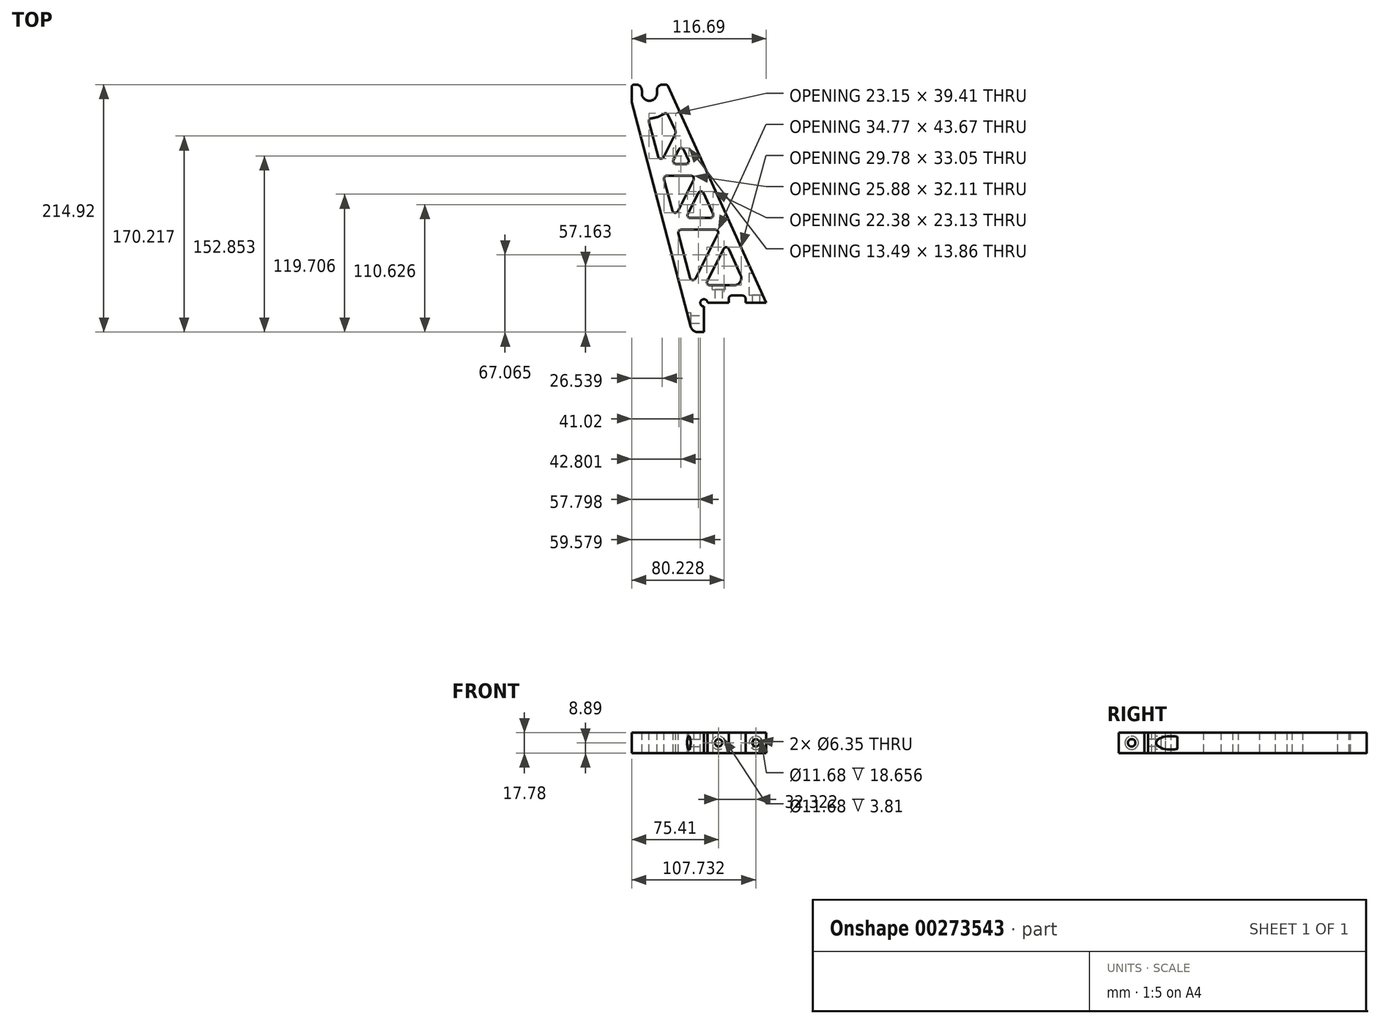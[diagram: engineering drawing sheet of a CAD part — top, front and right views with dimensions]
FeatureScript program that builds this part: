
annotation { "Feature Type Name" : "Feature", "Feature Type Description" : "" }
export const myFeature = defineFeature(function(context is Context, id is Id, definition is map)
    precondition{}
    {
        {
            var Q0;
            Q0=qCreatedBy(makeId("Top.planeOp"),FACE);
            var sketch = newSketch(context, id + "F0", { "sketchPlane" : qUnion([Q0])});
            skLineSegment(sketch, "E0", {"start": v(3.18, 0) * mm, "end": v(60.33, 0) * mm, "construction": true});
            skLineSegment(sketch, "E1", {"start": v(60.33, 0) * mm, "end": v(60.33, 190.5) * mm, "construction": true});
            skCircle(sketch, "E2", {"center": v(-47.28, 181.9) * mm, "radius": 101.6 * mm, "construction": true});
            skLineSegment(sketch, "E3.bottom", {"start": v(60.33, 0) * mm, "end": v(3.18, 0) * mm, "construction": true});
            skLineSegment(sketch, "E3.top", {"start": v(60.32, 220) * mm, "end": v(-79.68, 220) * mm, "construction": true});
            skLineSegment(sketch, "E3.left", {"start": v(60.33, 0) * mm, "end": v(60.33, 220) * mm, "construction": true});
            skLineSegment(sketch, "E3.right", {"start": v(-79.67, 0) * mm, "end": v(-79.68, 220) * mm, "construction": true});
            skArc(sketch, "E4", {"start": v(-53.82, 181.9) * mm, "mid": v(-47.28, 175.36) * mm, "end": v(-40.74, 181.9) * mm});
            skLineSegment(sketch, "E5", {"start": v(-53.82, 181.9) * mm, "end": v(-53.82, 184.44) * mm});
            skLineSegment(sketch, "E6", {"start": v(-40.74, 181.9) * mm, "end": v(-40.74, 184.44) * mm});
            skLineSegment(sketch, "E7", {"start": v(-35.66, 189.52) * mm, "end": v(-33.49, 189.52) * mm});
            skLineSegment(sketch, "E8", {"start": v(-31.18, 188.03) * mm, "end": v(53.98, 0) * mm});
            skLineSegment(sketch, "E9", {"start": v(53.98, 0) * mm, "end": v(36.07, 0) * mm});
            skLineSegment(sketch, "E10", {"start": v(36.07, 0) * mm, "end": v(36.07, 3.81) * mm});
            skLineSegment(sketch, "E11", {"start": v(33.53, 6.35) * mm, "end": v(24.13, 6.35) * mm});
            skLineSegment(sketch, "E12", {"start": v(21.59, 3.81) * mm, "end": v(21.59, 0) * mm});
            skLineSegment(sketch, "E13", {"start": v(21.59, 0) * mm, "end": v(3.18, 0) * mm});
            skLineSegment(sketch, "E14", {"start": v(0, -25.4) * mm, "end": v(-5.26, -25.4) * mm});
            skLineSegment(sketch, "E15", {"start": v(-11.4, -20.67) * mm, "end": v(-62.71, 174.28) * mm});
            skLineSegment(sketch, "E16", {"start": v(-62.71, 174.28) * mm, "end": v(-62.71, 186.98) * mm});
            skLineSegment(sketch, "E17", {"start": v(-60.17, 189.52) * mm, "end": v(-58.9, 189.52) * mm});
            skLineSegment(sketch, "E18", {"start": v(0, -3.18) * mm, "end": v(0, -25.4) * mm});
            skArc(sketch, "E19", {"start": v(3.18, 0) * mm, "mid": v(-2.25, 2.25) * mm, "end": v(0, -3.18) * mm});
            skLineSegment(sketch, "E20.trimOffspring", {"start": v(0, 0) * mm, "end": v(-79.67, 0) * mm, "construction": true});
            skPoint(sketch, "E21.visualSharp", {"position": v(-53.82, 189.52) * mm});
            skArc(sketch, "E21.filletArc", {"start": v(-53.82, 184.44) * mm, "mid": v(-55.31, 188.03) * mm, "end": v(-58.9, 189.52) * mm});
            skPoint(sketch, "E22.visualSharp", {"position": v(-40.74, 189.52) * mm});
            skArc(sketch, "E22.filletArc", {"start": v(-35.66, 189.52) * mm, "mid": v(-39.25, 188.03) * mm, "end": v(-40.74, 184.44) * mm});
            skPoint(sketch, "E23.visualSharp", {"position": v(-62.71, 189.52) * mm});
            skArc(sketch, "E23.filletArc", {"start": v(-60.17, 189.52) * mm, "mid": v(-61.97, 188.78) * mm, "end": v(-62.71, 186.98) * mm});
            skPoint(sketch, "E24.visualSharp", {"position": v(-31.85, 189.52) * mm});
            skArc(sketch, "E24.filletArc", {"start": v(-31.18, 188.03) * mm, "mid": v(-32.11, 189.11) * mm, "end": v(-33.49, 189.52) * mm});
            skPoint(sketch, "E25.visualSharp", {"position": v(-10.16, -25.4) * mm});
            skArc(sketch, "E25.filletArc", {"start": v(-11.4, -20.67) * mm, "mid": v(-9.14, -24.08) * mm, "end": v(-5.26, -25.4) * mm});
            skLineSegment(sketch, "E26", {"start": v(-47.66, 157.02) * mm, "end": v(-39.76, 127) * mm});
            skLineSegment(sketch, "E27", {"start": v(5.17, 15.24) * mm, "end": v(26.07, 15.24) * mm});
            skLineSegment(sketch, "E28", {"start": v(31.86, 24.2) * mm, "end": v(21.63, 46.8) * mm});
            skArc(sketch, "E29", {"start": v(-45.42, 160.2) * mm, "mid": v(-39.85, 161.43) * mm, "end": v(-34.78, 164.06) * mm});
            skLineSegment(sketch, "E30", {"start": v(-7.33, 21.2) * mm, "end": v(12.2, 59.81) * mm});
            skLineSegment(sketch, "E31", {"start": v(9.93, 63.5) * mm, "end": v(-19.76, 63.5) * mm});
            skLineSegment(sketch, "E32", {"start": v(17.05, 46.9) * mm, "end": v(2.9, 18.93) * mm});
            skLineSegment(sketch, "E33", {"start": v(-11.78, 73.66) * mm, "end": v(5.53, 73.66) * mm});
            skLineSegment(sketch, "E34", {"start": v(-22.7, 79.63) * mm, "end": v(-9.02, 106.68) * mm});
            skLineSegment(sketch, "E35", {"start": v(-14.05, 77.35) * mm, "end": v(-4.92, 95.4) * mm});
            skLineSegment(sketch, "E36", {"start": v(0, 13.2) * mm, "end": v(-31.6, 133.28) * mm, "construction": true});
            skLineSegment(sketch, "E37", {"start": v(-11.29, 110.36) * mm, "end": v(-32.09, 110.36) * mm});
            skLineSegment(sketch, "E38", {"start": v(-15.7, 120.52) * mm, "end": v(-24.12, 120.52) * mm});
            skLineSegment(sketch, "E39", {"start": v(-26.38, 124.2) * mm, "end": v(-21.94, 133) * mm});
            skLineSegment(sketch, "E40", {"start": v(-35.04, 126.5) * mm, "end": v(-25, 146.32) * mm});
            skLineSegment(sketch, "E41.trimOffspring", {"start": v(7.84, 77.25) * mm, "end": v(-0.34, 95.3) * mm});
            skLineSegment(sketch, "E42.trimOffspring", {"start": v(-22.21, 60.31) * mm, "end": v(-12.05, 21.7) * mm});
            skLineSegment(sketch, "E43.trimOffspring", {"start": v(-34.55, 107.18) * mm, "end": v(-27.43, 80.13) * mm});
            skLineSegment(sketch, "E44.trimOffspring", {"start": v(-13.38, 124.11) * mm, "end": v(-17.36, 132.9) * mm});
            skLineSegment(sketch, "E45.trimOffspring", {"start": v(-24.93, 149.62) * mm, "end": v(-31, 163.03) * mm});
            skPoint(sketch, "E46.visualSharp", {"position": v(-32.37, 166.03) * mm});
            skArc(sketch, "E46.filletArc", {"start": v(-31, 163.03) * mm, "mid": v(-32.65, 164.43) * mm, "end": v(-34.78, 164.06) * mm});
            skPoint(sketch, "E47.visualSharp", {"position": v(-48.49, 160.15) * mm});
            skArc(sketch, "E47.filletArc", {"start": v(-45.42, 160.2) * mm, "mid": v(-47.28, 159.13) * mm, "end": v(-47.66, 157.02) * mm});
            skPoint(sketch, "E48.visualSharp", {"position": v(-38.06, 120.52) * mm});
            skArc(sketch, "E48.filletArc", {"start": v(-39.76, 127) * mm, "mid": v(-37.57, 125.11) * mm, "end": v(-35.04, 126.5) * mm});
            skPoint(sketch, "E49.visualSharp", {"position": v(-24.18, 147.95) * mm});
            skArc(sketch, "E49.filletArc", {"start": v(-25, 146.32) * mm, "mid": v(-24.6, 147.96) * mm, "end": v(-24.93, 149.62) * mm});
            skPoint(sketch, "E50.visualSharp", {"position": v(-19.55, 137.72) * mm});
            skArc(sketch, "E50.filletArc", {"start": v(-17.36, 132.9) * mm, "mid": v(-19.62, 134.38) * mm, "end": v(-21.94, 133) * mm});
            skPoint(sketch, "E51.visualSharp", {"position": v(-28.25, 120.52) * mm});
            skArc(sketch, "E51.filletArc", {"start": v(-26.38, 124.2) * mm, "mid": v(-26.28, 121.73) * mm, "end": v(-24.12, 120.52) * mm});
            skPoint(sketch, "E52.visualSharp", {"position": v(-11.76, 120.52) * mm});
            skArc(sketch, "E52.filletArc", {"start": v(-15.7, 120.52) * mm, "mid": v(-13.56, 121.69) * mm, "end": v(-13.38, 124.11) * mm});
            skPoint(sketch, "E53.visualSharp", {"position": v(-7.16, 110.36) * mm});
            skArc(sketch, "E53.filletArc", {"start": v(-9.02, 106.68) * mm, "mid": v(-9.12, 109.15) * mm, "end": v(-11.29, 110.36) * mm});
            skPoint(sketch, "E54.visualSharp", {"position": v(-2.52, 100.13) * mm});
            skArc(sketch, "E54.filletArc", {"start": v(-0.34, 95.3) * mm, "mid": v(-2.6, 96.8) * mm, "end": v(-4.92, 95.4) * mm});
            skPoint(sketch, "E55.visualSharp", {"position": v(-15.91, 73.66) * mm});
            skArc(sketch, "E55.filletArc", {"start": v(-14.05, 77.35) * mm, "mid": v(-13.95, 74.87) * mm, "end": v(-11.78, 73.66) * mm});
            skPoint(sketch, "E56.visualSharp", {"position": v(9.46, 73.66) * mm});
            skArc(sketch, "E56.filletArc", {"start": v(5.53, 73.66) * mm, "mid": v(7.66, 74.82) * mm, "end": v(7.84, 77.25) * mm});
            skPoint(sketch, "E57.visualSharp", {"position": v(-25.72, 73.66) * mm});
            skArc(sketch, "E57.filletArc", {"start": v(-27.43, 80.13) * mm, "mid": v(-25.24, 78.25) * mm, "end": v(-22.7, 79.63) * mm});
            skPoint(sketch, "E58.visualSharp", {"position": v(-23.05, 63.5) * mm});
            skArc(sketch, "E58.filletArc", {"start": v(-19.76, 63.5) * mm, "mid": v(-21.77, 62.51) * mm, "end": v(-22.21, 60.31) * mm});
            skPoint(sketch, "E59.visualSharp", {"position": v(14.06, 63.5) * mm});
            skArc(sketch, "E59.filletArc", {"start": v(12.2, 59.81) * mm, "mid": v(12.1, 62.3) * mm, "end": v(9.93, 63.5) * mm});
            skPoint(sketch, "E60.visualSharp", {"position": v(-10.35, 15.24) * mm});
            skArc(sketch, "E60.filletArc", {"start": v(-12.05, 21.7) * mm, "mid": v(-9.86, 19.83) * mm, "end": v(-7.33, 21.2) * mm});
            skPoint(sketch, "E61.newPointA", {"position": v(0, 13.2) * mm});
            skArc(sketch, "E61.filletArc", {"start": v(2.9, 18.93) * mm, "mid": v(3, 16.45) * mm, "end": v(5.17, 15.24) * mm});
            skPoint(sketch, "E62.visualSharp", {"position": v(19.44, 51.62) * mm});
            skArc(sketch, "E62.filletArc", {"start": v(21.63, 46.8) * mm, "mid": v(19.37, 48.29) * mm, "end": v(17.05, 46.9) * mm});
            skPoint(sketch, "E63.visualSharp", {"position": v(35.92, 15.24) * mm});
            skArc(sketch, "E63.filletArc", {"start": v(26.07, 15.24) * mm, "mid": v(31.41, 18.15) * mm, "end": v(31.86, 24.2) * mm});
            skPoint(sketch, "E64.visualSharp", {"position": v(-35.38, 110.36) * mm});
            skArc(sketch, "E64.filletArc", {"start": v(-32.09, 110.36) * mm, "mid": v(-34.1, 109.37) * mm, "end": v(-34.55, 107.18) * mm});
            skPoint(sketch, "E65.visualSharp", {"position": v(21.6, 6.35) * mm});
            skArc(sketch, "E65.filletArc", {"start": v(24.13, 6.35) * mm, "mid": v(22.33, 5.6) * mm, "end": v(21.59, 3.81) * mm});
            skPoint(sketch, "E66.visualSharp", {"position": v(36.07, 6.35) * mm});
            skArc(sketch, "E66.filletArc", {"start": v(36.07, 3.81) * mm, "mid": v(35.32, 5.6) * mm, "end": v(33.53, 6.35) * mm});
            skLineSegment(sketch, "E67.bottom", {"start": v(3.18, 0) * mm, "end": v(21.59, 0) * mm});
            skLineSegment(sketch, "E67.top", {"start": v(3.18, 3.81) * mm, "end": v(21.59, 3.81) * mm});
            skLineSegment(sketch, "E67.left", {"start": v(3.18, 0) * mm, "end": v(3.18, 3.81) * mm});
            skLineSegment(sketch, "E67.right", {"start": v(21.59, 0) * mm, "end": v(21.59, 3.81) * mm});
            skLineSegment(sketch, "E68", {"start": v(36.07, 3.81) * mm, "end": v(52.25, 3.81) * mm});
            skLineSegment(sketch, "E69.top", {"start": v(0, -25.4) * mm, "end": v(-2.54, -25.4) * mm});
            skSolve(sketch);
        }
        {
            var Q0;
            Q0 = qSketchRegion(id + "F0", true);
            extrude(context, id + "F1", {"entities" : qUnion([Q0]), "oppositeDirection" : true, "depth" : 17.78 * mm});
        }
        {
            var Q0;
            Q0=makeQuery(id+"F1.opExtrude","SWEPT_FACE",FACE,{"disambiguationData":[OSD([sQuery(id+"F0.wireOp",EDGE,"E18")])]});
            var sketch = newSketch(context, id + "F2", { "sketchPlane" : qUnion([Q0])});
            skCircle(sketch, "E70", {"center": v(-14.29, -8.9) * mm, "radius": 3.24 * mm});
            skPoint(sketch, "E70.centerSnap0", {"position": v(-25.4, -8.9) * mm});
            skPoint(sketch, "E70.centerSnap1", {"position": v(-14.29, 0) * mm});
            skCircle(sketch, "E71", {"center": v(-14.29, -8.9) * mm, "radius": 5.84 * mm});
            skSolve(sketch);
        }
        {
            var Q0;
            Q0 = qSketchRegion(id + "F2", true);
            var Q1;
            Q1=makeQuery(id+"F2.imprint","IMPRINT",FACE,{"disambiguationData":[TD([[makeQuery(id+"F2.imprint","IMPRINT",EDGE,{"derivedFrom":sQuery(id+"F2.wireOp",EDGE,"E70")}),1.0]])]});
            extrude(context, id + "F3", {"entities" : qUnion([Q0, Q1]), "operationType" : NewBodyOperationType.REMOVE, "oppositeDirection" : true, "depth" : 25.4 * mm});
        }
        {
            var Q0;
            Q0=makeQuery(id+"F1.opExtrude","SWEPT_FACE",FACE,{"disambiguationData":[OSD([sQuery(id+"F0.wireOp",EDGE,"E9")])]});
            var sketch = newSketch(context, id + "F4", { "sketchPlane" : qUnion([Q0])});
            skCircle(sketch, "E72", {"center": v(45.02, -8.9) * mm, "radius": 3.18 * mm});
            skPoint(sketch, "E72.centerSnap0", {"position": v(53.98, -8.9) * mm});
            skPoint(sketch, "E72.centerSnap1", {"position": v(45.02, 0) * mm});
            skCircle(sketch, "E73", {"center": v(12.7, -8.9) * mm, "radius": 3.18 * mm});
            skPoint(sketch, "E73.centerSnap0", {"position": v(36.07, -8.9) * mm});
            skCircle(sketch, "E74", {"center": v(12.7, -8.9) * mm, "radius": 5.84 * mm});
            skCircle(sketch, "E75", {"center": v(45.02, -8.9) * mm, "radius": 5.84 * mm});
            skSolve(sketch);
        }
        {
            var Q0;
            Q0 = qSketchRegion(id + "F4", true);
            var Q1;
            Q1=makeQuery(id+"F4.imprint","IMPRINT",FACE,{"disambiguationData":[TD([[makeQuery(id+"F4.imprint","IMPRINT",EDGE,{"derivedFrom":sQuery(id+"F4.wireOp",EDGE,"E73")}),1.0]])]});
            var Q2;
            Q2=makeQuery(id+"F4.imprint","IMPRINT",FACE,{"disambiguationData":[TD([[makeQuery(id+"F4.imprint","IMPRINT",EDGE,{"derivedFrom":sQuery(id+"F4.wireOp",EDGE,"E72")}),1.0]])]});
            extrude(context, id + "F5", {"entities" : qUnion([Q0, Q1, Q2]), "operationType" : NewBodyOperationType.REMOVE, "oppositeDirection" : true, "depth" : 25.4 * mm});
        }
        {
            var Q0;
            Q0=makeQuery(id+"F4.imprint","IMPRINT",FACE,{"disambiguationData":[TD([[makeQuery(id+"F4.imprint","IMPRINT",EDGE,{"derivedFrom":sQuery(id+"F4.wireOp",EDGE,"E73")}),-1.0]])]});
            extrude(context, id + "F6", {"entities" : qUnion([Q0]), "operationType" : NewBodyOperationType.ADD, "oppositeDirection" : true, "depth" : 11.43 * mm});
        }
        {
            var Q0;
            Q0=makeQuery(id+"F4.imprint","IMPRINT",FACE,{"disambiguationData":[TD([[makeQuery(id+"F4.imprint","IMPRINT",EDGE,{"derivedFrom":sQuery(id+"F4.wireOp",EDGE,"E72")}),-1.0]])]});
            var Q1;
            Q1=makeQuery(id+"F5.boolean.opBoolean","COPY",FACE,{"derivedFrom":makeQuery(id+"F5.opExtrude","SWEPT_FACE",FACE,{"disambiguationData":[OSD([sQuery(id+"F4.wireOp",EDGE,"E75")])]})});
            extrude(context, id + "F7", {"entities" : qUnion([Q0]), "operationType" : NewBodyOperationType.ADD, "oppositeDirection" : true, "endBoundEntityFace" : qUnion([Q1]), "depth" : 6.74 * mm});
        }
        {
            var Q0;
            Q0=makeQuery(id+"F2.imprint","IMPRINT",FACE,{"disambiguationData":[TD([[makeQuery(id+"F2.imprint","IMPRINT",EDGE,{"derivedFrom":sQuery(id+"F2.wireOp",EDGE,"E70")}),-1.0]])]});
            var Q1;
            Q1=makeQuery(id+"F1.opExtrude","SWEPT_FACE",FACE,{"disambiguationData":[OSD([sQuery(id+"F0.wireOp",EDGE,"E15")])]});
            extrude(context, id + "F8", {"entities" : qUnion([Q0]), "operationType" : NewBodyOperationType.ADD, "oppositeDirection" : true, "endBoundEntityFace" : qUnion([Q1]), "depth" : 11.43 * mm});
        }
    });
